FCSTD DOCUMENT  (FreeCAD 0.18R16131 (Git))
Label: Turnstile_V3.1
License: All rights reserved
LicenseURL: http://en.wikipedia.org/wiki/All_rights_reserved
objects: Sketcher::SketchObject×3, PartDesign::Body×2, App::Part×2, PartDesign::Pad×1
note: 7 computed .brp shape members not serialized (recipe doc carries the construction recipe); baked Part::Feature solids carry a one-line shape summary decoded from their .brp

FEATURE [Sketcher::SketchObject] Sketch
  MapMode = 2
  sketch-geometry (32):
    g0: LineSegment StartX=5 StartY=20 StartZ=0 EndX=-5 EndY=20 EndZ=0
    g1: LineSegment StartX=-5 StartY=20 StartZ=0 EndX=-20 EndY=5 EndZ=0
    g2: LineSegment StartX=-20 StartY=5 StartZ=0 EndX=-20 EndY=-5 EndZ=0
    g3: LineSegment StartX=-20 StartY=-5 StartZ=0 EndX=-5 EndY=-20 EndZ=0
    g4: LineSegment StartX=-5 StartY=-20 StartZ=0 EndX=5 EndY=-20 EndZ=0
    g5: LineSegment StartX=5 StartY=-20 StartZ=0 EndX=20 EndY=-5 EndZ=0
    g6: LineSegment StartX=20 StartY=-5 StartZ=0 EndX=20 EndY=5 EndZ=0
    g7: LineSegment StartX=20 StartY=5 StartZ=0 EndX=5 EndY=20 EndZ=0
    g8: LineSegment StartX=-5 StartY=20 StartZ=0 EndX=-5 EndY=28 EndZ=0
    g9: LineSegment StartX=-5 StartY=28 StartZ=0 EndX=5 EndY=28 EndZ=0
    g10: LineSegment StartX=5 StartY=28 StartZ=0 EndX=5 EndY=20 EndZ=0
    g11: LineSegment StartX=20 StartY=5 StartZ=0 EndX=28 EndY=5 EndZ=0
    g12: LineSegment StartX=28 StartY=5 StartZ=0 EndX=28 EndY=-5 EndZ=0
    g13: LineSegment StartX=28 StartY=-5 StartZ=0 EndX=20 EndY=-5 EndZ=0
    g14: LineSegment StartX=-5 StartY=-20 StartZ=0 EndX=-5 EndY=-28 EndZ=0
    g15: LineSegment StartX=-5 StartY=-28 StartZ=0 EndX=5 EndY=-28 EndZ=0
    g16: LineSegment StartX=5 StartY=-28 StartZ=0 EndX=5 EndY=-20 EndZ=0
    g17: LineSegment StartX=-20 StartY=5 StartZ=0 EndX=-28 EndY=5 EndZ=0
    g18: LineSegment StartX=-28 StartY=5 StartZ=0 EndX=-28 EndY=-5 EndZ=0
    g19: LineSegment StartX=-28 StartY=-5 StartZ=0 EndX=-20 EndY=-5 EndZ=0
    g20: GeomPoint X=-24 Y=5 Z=0
    g21: GeomPoint X=-24 Y=-5 Z=0
    g22: GeomPoint X=-5 Y=24 Z=0
    g23: LineSegment StartX=-5 StartY=24 StartZ=0 EndX=-24 EndY=5 EndZ=0
    g24: GeomPoint X=5 Y=24 Z=0
    g25: GeomPoint X=24 Y=5 Z=0
    g26: LineSegment StartX=5 StartY=24 StartZ=0 EndX=24 EndY=5 EndZ=0
    g27: GeomPoint X=24 Y=-5 Z=0
    g28: GeomPoint X=-5 Y=-24 Z=0
    g29: GeomPoint X=5 Y=-24 Z=0
    g30: LineSegment StartX=-5 StartY=-24 StartZ=0 EndX=-24 EndY=-5 EndZ=0
    g31: LineSegment StartX=5 StartY=-24 StartZ=0 EndX=24 EndY=-5 EndZ=0
  constraints (72):
    c: Coincident(g0,g1)
    c: Coincident(g1,g2)
    c: Coincident(g2,g3)
    c: Coincident(g3,g4)
    c: Coincident(g4,g5)
    c: Coincident(g5,g6)
    c: Coincident(g6,g7)
    c: Coincident(g7,g0)
    c: Symmetric(g0,g0,g-2)
    c: Symmetric(g4,g3,g-2)
    c: Symmetric(g5,g6,g-1)
    c: Symmetric(g1,g2,g-1)
    c: DistanceY(g-1,g0) = 20
    c: DistanceX(g-1,g5) = 20
    c: DistanceY(g4,g-1) = 20
    c: DistanceX(g1,g-1) = 20
    c: DistanceX(g0,g0) = 10
    c: DistanceY(g5,g6) = 10
    c: DistanceX(g3,g4) = 10
    c: DistanceY(g2,g1) = 10
    c: Coincident(g8,g9)
    c: Coincident(g9,g10)
    c: Symmetric(g9,g8,g-2)
    c: Vertical(g8)
    c: Coincident(g8,g0)
    c: Coincident(g10,g0)
    c: DistanceY(g0,g9) = 8
    c: Coincident(g11,g12)
    c: Coincident(g12,g13)
    c: Symmetric(g11,g12,g-1)
    c: Horizontal(g11)
    c: Coincident(g11,g6)
    c: Coincident(g13,g5)
    c: DistanceX(g6,g11) = 8
    c: Coincident(g14,g15)
    c: Coincident(g15,g16)
    c: Symmetric(g14,g15,g-2)
    c: Vertical(g16)
    c: Coincident(g16,g4)
    c: Coincident(g14,g3)
    c: DistanceY(g15,g4) = 8
    c: Coincident(g17,g18)
    c: Coincident(g18,g19)
    c: Coincident(g19,g2)
    c: Symmetric(g17,g18,g-1)
    c: Coincident(g17,g1)
    c: Horizontal(g17)
    c: DistanceX(g18,g2) = 8
    c: PointOnObject(g20,g17)
    c: PointOnObject(g21,g19)
    c: PointOnObject(g22,g8)
    c: PointOnObject(g24,g10)
    c: PointOnObject(g25,g11)
    c: PointOnObject(g27,g13)
    c: PointOnObject(g28,g14)
    c: PointOnObject(g29,g16)
    c: Coincident(g31,g29)
    c: Coincident(g30,g21)
    c: Coincident(g31,g27)
    c: Coincident(g23,g20)
    c: Coincident(g28,g30)
    c: Coincident(g26,g25)
    c: Coincident(g23,g22)
    c: Coincident(g24,g26)
    c: DistanceY(g0,g22) = 4
    c: DistanceY(g0,g24) = 4
    c: DistanceX(g20,g1) = 4
    c: DistanceX(g21,g2) = 4
    c: DistanceX(g6,g25) = 4
    c: DistanceX(g5,g27) = 4
    c: DistanceY(g28,g3) = 4
    c: DistanceY(g29,g4) = 4
FEATURE [PartDesign::Body] Body001
  Group = -> [Sketch]
  Origin = -> Origin003
FEATURE [App::Part] Part001
  Group = -> [Body001]
  Origin = -> Origin002
FEATURE [Sketcher::SketchObject] Sketch001
  MapMode = 2
  sketch-geometry (24):
    g0: LineSegment StartX=-5 StartY=28 StartZ=0 EndX=5 EndY=28 EndZ=0
    g1: LineSegment StartX=28 StartY=5 StartZ=0 EndX=28 EndY=-5 EndZ=0
    g2: LineSegment StartX=-5 StartY=-28 StartZ=0 EndX=5 EndY=-28 EndZ=0
    g3: LineSegment StartX=-28 StartY=5 StartZ=0 EndX=-28 EndY=-5 EndZ=0
    g4: GeomPoint X=-24 Y=5 Z=0
    g5: GeomPoint X=-24 Y=-5 Z=0
    g6: GeomPoint X=-5 Y=24 Z=0
    g7: LineSegment StartX=-5 StartY=24 StartZ=0 EndX=-24 EndY=5 EndZ=0
    g8: GeomPoint X=5 Y=24 Z=0
    g9: GeomPoint X=24 Y=5 Z=0
    g10: LineSegment StartX=5 StartY=24 StartZ=0 EndX=24 EndY=5 EndZ=0
    g11: GeomPoint X=24 Y=-5 Z=0
    g12: GeomPoint X=-5 Y=-24 Z=0
    g13: GeomPoint X=5 Y=-24 Z=0
    g14: LineSegment StartX=-5 StartY=-24 StartZ=0 EndX=-24 EndY=-5 EndZ=0
    g15: LineSegment StartX=5 StartY=-24 StartZ=0 EndX=24 EndY=-5 EndZ=0
    g16: LineSegment StartX=-28 StartY=5 StartZ=0 EndX=-24 EndY=5 EndZ=0
    g17: LineSegment StartX=-28 StartY=-5 StartZ=0 EndX=-24 EndY=-5 EndZ=0
    g18: LineSegment StartX=-5 StartY=28 StartZ=0 EndX=-5 EndY=24 EndZ=0
    g19: LineSegment StartX=5 StartY=28 StartZ=0 EndX=5 EndY=24 EndZ=0
    g20: LineSegment StartX=24 StartY=5 StartZ=0 EndX=28 EndY=5 EndZ=0
    g21: LineSegment StartX=24 StartY=-5 StartZ=0 EndX=28 EndY=-5 EndZ=0
    g22: LineSegment StartX=5 StartY=-24 StartZ=0 EndX=5 EndY=-28 EndZ=0
    g23: LineSegment StartX=-5 StartY=-24 StartZ=0 EndX=-5 EndY=-28 EndZ=0
  constraints (52):
    c: Symmetric(g0,g0,g-2)
    c: Symmetric(g1,g1,g-1)
    c: Symmetric(g2,g2,g-2)
    c: Symmetric(g3,g3,g-1)
    c: Coincident(g15,g13)
    c: Coincident(g14,g5)
    c: Coincident(g15,g11)
    c: Coincident(g7,g4)
    c: Coincident(g12,g14)
    c: Coincident(g10,g9)
    c: Coincident(g7,g6)
    c: Coincident(g8,g10)
    c: Horizontal(g16)
    c: Horizontal(g17)
    c: Coincident(g16,g4)
    c: Coincident(g17,g5)
    c: Coincident(g18,g0)
    c: Coincident(g18,g6)
    c: Coincident(g8,g19)
    c: Coincident(g19,g0)
    c: Coincident(g9,g20)
    c: Coincident(g1,g20)
    c: Coincident(g11,g21)
    c: Coincident(g21,g1)
    c: Coincident(g23,g12)
    c: Coincident(g23,g2)
    c: Coincident(g13,g22)
    c: Coincident(g22,g2)
    c: Coincident(g3,g16)
    c: Coincident(g3,g17)
    c: DistanceX(g3,g-1) = 28
    c: DistanceY(g-1,g0) = 28
    c: DistanceY(g2,g-1) = 28
    c: DistanceX(g-1,g1) = 28
    c: Vertical(g18)
    c: Vertical(g19)
    c: Vertical(g23)
    c: Vertical(g22)
    c: Horizontal(g20)
    c: Horizontal(g21)
    c: DistanceX(g4,g-1) = 24
    c: DistanceX(g5,g-1) = 24
    c: DistanceX(g-1,g9) = 24
    c: DistanceX(g-1,g11) = 24
    c: DistanceY(g12,g-1) = 24
    c: DistanceY(g13,g-1) = 24
    c: DistanceY(g-1,g6) = 24
    c: DistanceY(g-1,g8) = 24
    c: DistanceX(g0,g0) = 10
    c: DistanceX(g2,g2) = 10
    c: DistanceY(g3,g3) = 10
    c: DistanceY(g1,g1) = 10
FEATURE [Sketcher::SketchObject] CopySketch
  sketch-geometry (32):
    g0: LineSegment StartX=5 StartY=20 StartZ=0 EndX=-5 EndY=20 EndZ=0
    g1: LineSegment StartX=-5 StartY=20 StartZ=0 EndX=-20 EndY=5 EndZ=0
    g2: LineSegment StartX=-20 StartY=5 StartZ=0 EndX=-20 EndY=-5 EndZ=0
    g3: LineSegment StartX=-20 StartY=-5 StartZ=0 EndX=-5 EndY=-20 EndZ=0
    g4: LineSegment StartX=-5 StartY=-20 StartZ=0 EndX=5 EndY=-20 EndZ=0
    g5: LineSegment StartX=5 StartY=-20 StartZ=0 EndX=20 EndY=-5 EndZ=0
    g6: LineSegment StartX=20 StartY=-5 StartZ=0 EndX=20 EndY=5 EndZ=0
    g7: LineSegment StartX=20 StartY=5 StartZ=0 EndX=5 EndY=20 EndZ=0
    g8: LineSegment StartX=-5 StartY=20 StartZ=0 EndX=-5 EndY=28 EndZ=0
    g9: LineSegment StartX=-5 StartY=28 StartZ=0 EndX=5 EndY=28 EndZ=0
    g10: LineSegment StartX=5 StartY=28 StartZ=0 EndX=5 EndY=20 EndZ=0
    g11: LineSegment StartX=20 StartY=5 StartZ=0 EndX=28 EndY=5 EndZ=0
    g12: LineSegment StartX=28 StartY=5 StartZ=0 EndX=28 EndY=-5 EndZ=0
    g13: LineSegment StartX=28 StartY=-5 StartZ=0 EndX=20 EndY=-5 EndZ=0
    g14: LineSegment StartX=-5 StartY=-20 StartZ=0 EndX=-5 EndY=-28 EndZ=0
    g15: LineSegment StartX=-5 StartY=-28 StartZ=0 EndX=5 EndY=-28 EndZ=0
    g16: LineSegment StartX=5 StartY=-28 StartZ=0 EndX=5 EndY=-20 EndZ=0
    g17: LineSegment StartX=-20 StartY=5 StartZ=0 EndX=-28 EndY=5 EndZ=0
    g18: LineSegment StartX=-28 StartY=5 StartZ=0 EndX=-28 EndY=-5 EndZ=0
    g19: LineSegment StartX=-28 StartY=-5 StartZ=0 EndX=-20 EndY=-5 EndZ=0
    g20: GeomPoint X=-24 Y=5 Z=0
    g21: GeomPoint X=-24 Y=-5 Z=0
    g22: GeomPoint X=-5 Y=24 Z=0
    g23: LineSegment StartX=-5 StartY=24 StartZ=0 EndX=-24 EndY=5 EndZ=0
    g24: GeomPoint X=5 Y=24 Z=0
    g25: GeomPoint X=24 Y=5 Z=0
    g26: LineSegment StartX=5 StartY=24 StartZ=0 EndX=24 EndY=5 EndZ=0
    g27: GeomPoint X=24 Y=-5 Z=0
    g28: GeomPoint X=-5 Y=-24 Z=0
    g29: GeomPoint X=5 Y=-24 Z=0
    g30: LineSegment StartX=-5 StartY=-24 StartZ=0 EndX=-24 EndY=-5 EndZ=0
    g31: LineSegment StartX=5 StartY=-24 StartZ=0 EndX=24 EndY=-5 EndZ=0
  constraints (72):
    c: Coincident(g0,g1)
    c: Coincident(g1,g2)
    c: Coincident(g2,g3)
    c: Coincident(g3,g4)
    c: Coincident(g4,g5)
    c: Coincident(g5,g6)
    c: Coincident(g6,g7)
    c: Coincident(g7,g0)
    c: Symmetric(g0,g0,g-2)
    c: Symmetric(g4,g3,g-2)
    c: Symmetric(g5,g6,g-1)
    c: Symmetric(g1,g2,g-1)
    c: DistanceY(g-1,g0) = 20
    c: DistanceX(g-1,g5) = 20
    c: DistanceY(g4,g-1) = 20
    c: DistanceX(g1,g-1) = 20
    c: DistanceX(g0,g0) = 10
    c: DistanceY(g5,g6) = 10
    c: DistanceX(g3,g4) = 10
    c: DistanceY(g2,g1) = 10
    c: Coincident(g8,g9)
    c: Coincident(g9,g10)
    c: Symmetric(g9,g8,g-2)
    c: Vertical(g8)
    c: Coincident(g8,g0)
    c: Coincident(g10,g0)
    c: DistanceY(g0,g9) = 8
    c: Coincident(g11,g12)
    c: Coincident(g12,g13)
    c: Symmetric(g11,g12,g-1)
    c: Horizontal(g11)
    c: Coincident(g11,g6)
    c: Coincident(g13,g5)
    c: DistanceX(g6,g11) = 8
    c: Coincident(g14,g15)
    c: Coincident(g15,g16)
    c: Symmetric(g14,g15,g-2)
    c: Vertical(g16)
    c: Coincident(g16,g4)
    c: Coincident(g14,g3)
    c: DistanceY(g15,g4) = 8
    c: Coincident(g17,g18)
    c: Coincident(g18,g19)
    c: Coincident(g19,g2)
    c: Symmetric(g17,g18,g-1)
    c: Coincident(g17,g1)
    c: Horizontal(g17)
    c: DistanceX(g18,g2) = 8
    c: PointOnObject(g20,g17)
    c: PointOnObject(g21,g19)
    c: PointOnObject(g22,g8)
    c: PointOnObject(g24,g10)
    c: PointOnObject(g25,g11)
    c: PointOnObject(g27,g13)
    c: PointOnObject(g28,g14)
    c: PointOnObject(g29,g16)
    c: Coincident(g31,g29)
    c: Coincident(g30,g21)
    c: Coincident(g31,g27)
    c: Coincident(g23,g20)
    c: Coincident(g28,g30)
    c: Coincident(g26,g25)
    c: Coincident(g23,g22)
    c: Coincident(g24,g26)
    c: DistanceY(g0,g22) = 4
    c: DistanceY(g0,g24) = 4
    c: DistanceX(g20,g1) = 4
    c: DistanceX(g21,g2) = 4
    c: DistanceX(g6,g25) = 4
    c: DistanceX(g5,g27) = 4
    c: DistanceY(g28,g3) = 4
    c: DistanceY(g29,g4) = 4
FEATURE [PartDesign::Pad] Pad
  Length = 10
  Length2 = 100
  Profile = -> CopySketch
  Type = 0
FEATURE [PartDesign::Body] Body
  Group = -> [CopySketch,Pad]
  Origin = -> Origin004
  Tip = -> Pad
FEATURE [App::Part] Part
  Group = -> [Body]
  Origin = -> Origin
